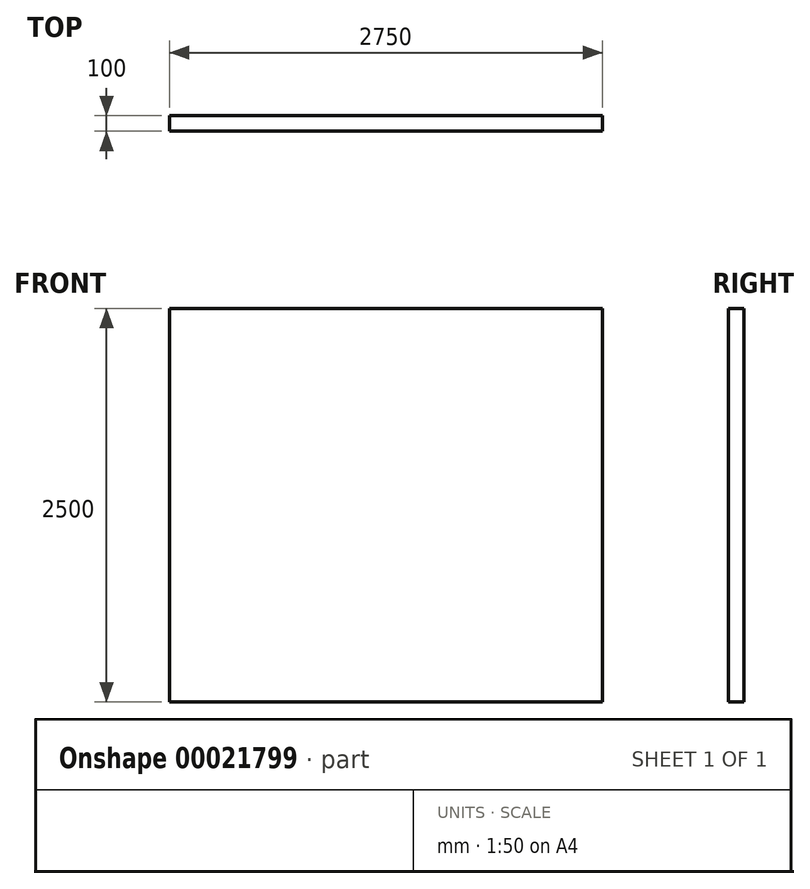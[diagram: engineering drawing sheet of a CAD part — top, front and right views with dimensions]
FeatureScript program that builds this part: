
annotation { "Feature Type Name" : "Feature", "Feature Type Description" : "" }
export const myFeature = defineFeature(function(context is Context, id is Id, definition is map)
    precondition{}
    {
        {
            var Q0;
            Q0=qCreatedBy(makeId("Top.planeOp"),FACE);
            var sketch = newSketch(context, id + "F0", { "sketchPlane" : qUnion([Q0])});
            skLineSegment(sketch, "E0.bottom", {"start": v(0, 0) * mm, "end": v(2750, 0) * mm});
            skLineSegment(sketch, "E0.top", {"start": v(0, 100) * mm, "end": v(2750, 100) * mm});
            skLineSegment(sketch, "E0.left", {"start": v(0, 0) * mm, "end": v(0, 100) * mm});
            skLineSegment(sketch, "E0.right", {"start": v(2750, 0) * mm, "end": v(2750, 100) * mm});
            skSolve(sketch);
        }
        {
            var Q0;
            Q0=makeQuery(id+"F0.imprint","IMPRINT",FACE,{"disambiguationData":[TD([[makeQuery(id+"F0.imprint","IMPRINT",EDGE,{"derivedFrom":sQuery(id+"F0.wireOp",EDGE,"E0.bottom")}),1.0]])]});
            extrude(context, id + "F1", {"entities" : qUnion([Q0]), "depth" : 2500 * mm});
        }
    });
